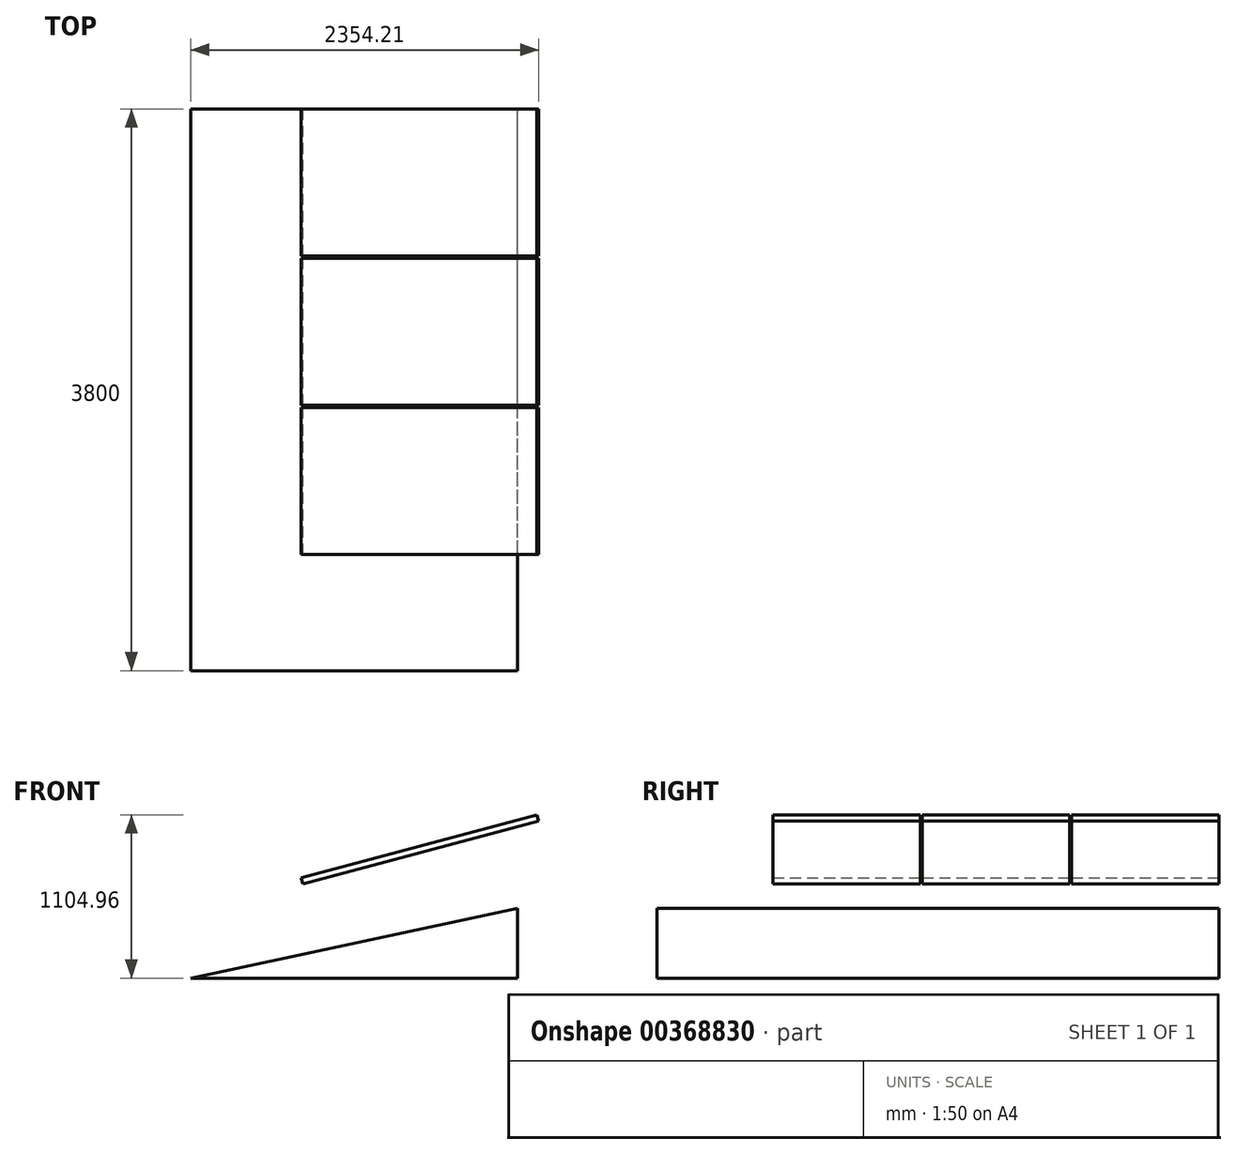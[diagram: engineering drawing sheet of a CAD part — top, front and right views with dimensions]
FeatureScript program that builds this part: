
annotation { "Feature Type Name" : "Feature", "Feature Type Description" : "" }
export const myFeature = defineFeature(function(context is Context, id is Id, definition is map)
    precondition{}
    {
        {
            var Q0;
            Q0=qCreatedBy(makeId("Front.planeOp"),FACE);
            var sketch = newSketch(context, id + "F0", { "sketchPlane" : qUnion([Q0])});
            skLineSegment(sketch, "E0", {"start": v(-73.26, 0) * mm, "end": v(2136.74, 0) * mm});
            skLineSegment(sketch, "E1", {"start": v(-73.26, 0) * mm, "end": v(2136.74, 472.76) * mm});
            skLineSegment(sketch, "E2", {"start": v(2136.74, 472.76) * mm, "end": v(2136.74, 0) * mm});
            skLineSegment(sketch, "E3", {"start": v(675.1, 679.7) * mm, "end": v(2269.35, 1104.96) * mm});
            skLineSegment(sketch, "E4", {"start": v(2269.35, 1104.96) * mm, "end": v(2280.95, 1061.48) * mm});
            skLineSegment(sketch, "E5", {"start": v(2280.95, 1061.48) * mm, "end": v(686.69, 636.21) * mm});
            skLineSegment(sketch, "E6", {"start": v(686.69, 636.21) * mm, "end": v(675.1, 679.7) * mm});
            skSolve(sketch);
        }
        {
            var Q0;
            Q0=makeQuery(id+"F0.imprint","IMPRINT",FACE,{"disambiguationData":[TD([[makeQuery(id+"F0.imprint","IMPRINT",EDGE,{"derivedFrom":sQuery(id+"F0.wireOp",EDGE,"E0")}),1.0]])]});
            extrude(context, id + "F1", {"entities" : qUnion([Q0]), "depth" : 3800 * mm});
        }
        {
            var Q0;
            Q0 = qSketchRegion(id + "F0", true);
            extrude(context, id + "F2", {"entities" : qUnion([Q0]), "operationType" : NewBodyOperationType.ADD, "depth" : 995 * mm});
        }
        {
            var Q0;
            Q0=makeQuery(id+"F2.opExtrude","SWEPT_BODY",BODY,{"disambiguationData":[OSD([sQuery(id+"F0.wireOp",EDGE,"E3"),sQuery(id+"F0.wireOp",EDGE,"E4"),sQuery(id+"F0.wireOp",EDGE,"E5"),sQuery(id+"F0.wireOp",EDGE,"E6")])]});
            transform(context, id + "F3", {"entities" : qUnion([Q0]), "transformType" : TransformType.TRANSLATION_3D, "dx" : 0 * mm, "dy" : -1010 * mm, "dz" : 0 * mm, "makeCopy" : true});
        }
        {
            var Q0;
            Q0=makeQuery(id+"F3.opPattern","COPY",BODY,{"derivedFrom":makeQuery(id+"F2.opExtrude","SWEPT_BODY",BODY,{"disambiguationData":[OSD([sQuery(id+"F0.wireOp",EDGE,"E3"),sQuery(id+"F0.wireOp",EDGE,"E4"),sQuery(id+"F0.wireOp",EDGE,"E5"),sQuery(id+"F0.wireOp",EDGE,"E6")])]}),"instanceName":"1"});
            transform(context, id + "F4", {"entities" : qUnion([Q0]), "transformType" : TransformType.TRANSLATION_3D, "dx" : 0 * mm, "dy" : -1010 * mm, "dz" : 0 * mm, "makeCopy" : true});
        }
    });
